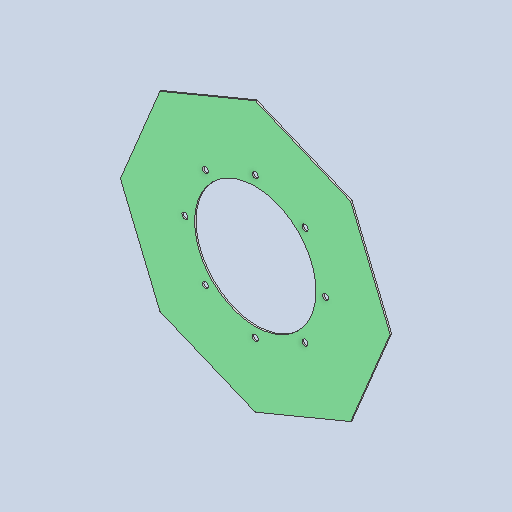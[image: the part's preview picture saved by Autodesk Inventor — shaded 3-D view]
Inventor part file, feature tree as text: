
AUTODESK INVENTOR PART (.ipt)
format: ipt  version: 2025 (Build 290162010, 162A)  size: 157,184 bytes
history: native  units: mm
features: sketch x2, other x2, sheet_metal_op x1, extrude x1, pattern_circular x1
ambient origin geometry x8: Origin, YZ Plane, XZ Plane, XY Plane, X Axis, Y Axis, Z Axis, Center Point
bodies: Solid1 (feature_tree)
feature tree (7):
  sheet_metal_op  "Face1"
  extrude  "Extrusion1"  Depth=3.0mm
  pattern_circular  "Circular Pattern1"  [2 undecoded]
  sketch  "Sketch2"  dims[d15=3.0mm d16=12.5mm]
  other  "Plate1"
  sketch  "Sketch4"  dims[d17=145.0mm d18=10.0mm d19=0.0mm d20=80.0mm d21=360.0deg d23=513.0mm d26=250.0mm]
  other  "Definition1"
note: 2 required parameter values undecoded (feature->parameter linkage not recoverable at this tier; creation-order binding heuristic only, values carry confidence <= 0.55)
